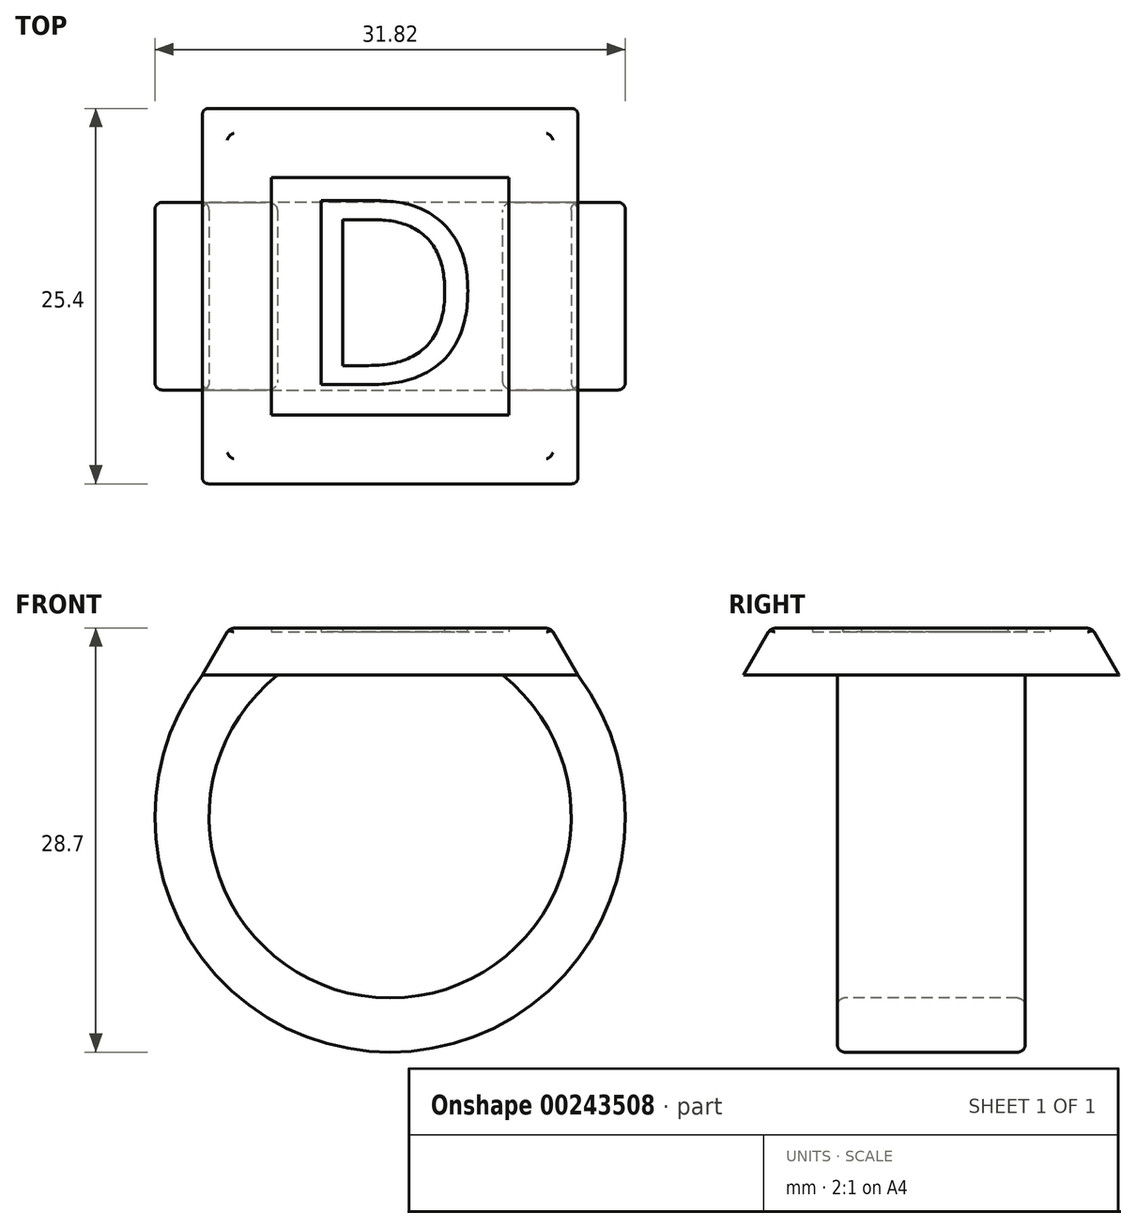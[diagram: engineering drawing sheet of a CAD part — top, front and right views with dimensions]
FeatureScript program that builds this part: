
annotation { "Feature Type Name" : "Feature", "Feature Type Description" : "" }
export const myFeature = defineFeature(function(context is Context, id is Id, definition is map)
    precondition{}
    {
        {
            var Q0;
            Q0=qCreatedBy(makeId("Top.planeOp"),FACE);
            var sketch = newSketch(context, id + "F0", { "sketchPlane" : qUnion([Q0])});
            skLineSegment(sketch, "E0.bottom", {"start": v(-12.7, 12.7) * mm, "end": v(12.7, 12.7) * mm});
            skLineSegment(sketch, "E0.top", {"start": v(-12.7, -12.7) * mm, "end": v(12.7, -12.7) * mm});
            skLineSegment(sketch, "E0.left", {"start": v(-12.7, 12.7) * mm, "end": v(-12.7, -12.7) * mm});
            skLineSegment(sketch, "E0.right", {"start": v(12.7, 12.7) * mm, "end": v(12.7, -12.7) * mm});
            skPoint(sketch, "E0.middle", {"position": v(0, 0) * mm});
            skSolve(sketch);
        }
        {
            var Q0;
            Q0=makeQuery(id+"F0.imprint","IMPRINT",FACE,{"disambiguationData":[TD([[makeQuery(id+"F0.imprint","IMPRINT",EDGE,{"derivedFrom":sQuery(id+"F0.wireOp",EDGE,"E0.bottom")}),-1.0]])]});
            extrude(context, id + "F1", {"entities" : qUnion([Q0]), "depth" : 3.17 * mm, "hasDraft" : true, "draftAngle" : 30 * degree, "draftPullDirection" : true});
        }
        {
            var Q0;
            Q0=qCreatedBy(makeId("Front.planeOp"),FACE);
            var sketch = newSketch(context, id + "F2", { "sketchPlane" : qUnion([Q0])});
            skArc(sketch, "E1", {"start": v(-10.16, 0) * mm, "mid": v(0, -23.56) * mm, "end": v(10.16, 0) * mm});
            skSolve(sketch);
        }
        {
            var Q0;
            Q0=makeQuery(id+"F1.opExtrude","CAP_FACE",FACE,{"disambiguationData":[OSD([sQuery(id+"F0.wireOp",EDGE,"E0.bottom"),sQuery(id+"F0.wireOp",EDGE,"E0.top"),sQuery(id+"F0.wireOp",EDGE,"E0.left"),sQuery(id+"F0.wireOp",EDGE,"E0.right")])],"isStart":true});
            var sketch = newSketch(context, id + "F3", { "sketchPlane" : qUnion([Q0])});
            skLineSegment(sketch, "E2.bottom", {"start": v(-12.7, -6.35) * mm, "end": v(-7.62, -6.35) * mm});
            skLineSegment(sketch, "E2.top", {"start": v(-12.7, 6.35) * mm, "end": v(-7.62, 6.35) * mm});
            skLineSegment(sketch, "E2.left", {"start": v(-12.7, -6.35) * mm, "end": v(-12.7, 6.35) * mm});
            skLineSegment(sketch, "E2.right", {"start": v(-7.62, -6.35) * mm, "end": v(-7.62, 6.35) * mm});
            skPoint(sketch, "E2.middle", {"position": v(-10.16, 0) * mm});
            skSolve(sketch);
        }
        {
            var Q0;
            Q0=makeQuery(id+"F3.imprint","IMPRINT",FACE,{"disambiguationData":[TD([[makeQuery(id+"F3.imprint","IMPRINT",EDGE,{"derivedFrom":sQuery(id+"F3.wireOp",EDGE,"E2.bottom")}),1.0]])]});
            var Q1;
            Q1=sQuery(id+"F2.wireOp",EDGE,"E1");
            sweep(context, id + "F4", {"operationType" : NewBodyOperationType.ADD, "profiles" : qUnion([Q0]), "path" : qUnion([Q1])});
        }
        {
            var Q0;
            Q0=qCreatedBy(makeId("Front.planeOp"),FACE);
            var sketch = newSketch(context, id + "F5", { "sketchPlane" : qUnion([Q0])});
            skLineSegment(sketch, "E3.0", {"start": v(7.62, 0) * mm, "end": v(10.16, 0) * mm});
            skLineSegment(sketch, "E4.0", {"start": v(10.01, -2.54) * mm, "end": v(10.16, 0) * mm});
            skArc(sketch, "E5", {"start": v(10.01, -2.54) * mm, "mid": v(8.9, -1.18) * mm, "end": v(7.62, 0) * mm});
            skSolve(sketch);
        }
        {
            var Q0;
            Q0=makeQuery(id+"F5.imprint","IMPRINT",FACE,{"disambiguationData":[TD([[makeQuery(id+"F5.imprint","IMPRINT",EDGE,{"derivedFrom":sQuery(id+"F5.wireOp",EDGE,"E3.0")}),-1.0]])]});
            extrude(context, id + "F6", {"entities" : qUnion([Q0]), "operationType" : NewBodyOperationType.ADD, "endBound" : BoundingType.SYMMETRIC, "depth" : 12.7 * mm});
        }
        {
            var Q0;
            Q0=makeQuery(id+"F1.opExtrude","CAP_EDGE",EDGE,{"disambiguationData":[OSD([sQuery(id+"F0.wireOp",EDGE,"E0.left")])],"isStart":false});
            var Q1;
            Q1=makeQuery(id+"F1.opExtrude","CAP_EDGE",EDGE,{"disambiguationData":[OSD([sQuery(id+"F0.wireOp",EDGE,"E0.right")])],"isStart":false});
            var Q2;
            Q2=makeQuery(id+"F1.opExtrude","CAP_EDGE",EDGE,{"disambiguationData":[OSD([sQuery(id+"F0.wireOp",EDGE,"E0.top")])],"isStart":false});
            var Q3;
            Q3=makeQuery(id+"F1.opExtrude","CAP_EDGE",EDGE,{"disambiguationData":[OSD([sQuery(id+"F0.wireOp",EDGE,"E0.bottom")])],"isStart":false});
            var Q4;
            Q4=makeQuery(id+"F1.opExtrude","SWEPT_EDGE",EDGE,{"disambiguationData":[OSD([sQuery(id+"F0.wireOp",EDGE,"E0.top"),sQuery(id+"F0.wireOp",EDGE,"E0.right")])]});
            var Q5;
            Q5=makeQuery(id+"F1.opExtrude","SWEPT_EDGE",EDGE,{"disambiguationData":[OSD([sQuery(id+"F0.wireOp",EDGE,"E0.top"),sQuery(id+"F0.wireOp",EDGE,"E0.left")])]});
            var Q6;
            Q6=makeQuery(id+"F1.opExtrude","SWEPT_EDGE",EDGE,{"disambiguationData":[OSD([sQuery(id+"F0.wireOp",EDGE,"E0.bottom"),sQuery(id+"F0.wireOp",EDGE,"E0.left")])]});
            var Q7;
            Q7=makeQuery(id+"F1.opExtrude","SWEPT_EDGE",EDGE,{"disambiguationData":[OSD([sQuery(id+"F0.wireOp",EDGE,"E0.bottom"),sQuery(id+"F0.wireOp",EDGE,"E0.right")])]});
            fillet(context, id + "F7", {"entities" : qUnion([Q0, Q1, Q2, Q3, Q4, Q5, Q6, Q7]), "radius" : 0.5 * mm, "tangentPropagation" : true, "allowEdgeOverflow" : false});
        }
        {
            var Q0;
            Q0=makeQuery(id+"F4.opSweep","SWEPT_EDGE",EDGE,{"disambiguationData":[OSD([sQuery(id+"F2.wireOp",EDGE,"E1"),sQuery(id+"F3.wireOp",EDGE,"E2.bottom"),sQuery(id+"F3.wireOp",EDGE,"E2.right")])]});
            var Q1;
            Q1=makeQuery(id+"F4.opSweep","SWEPT_EDGE",EDGE,{"disambiguationData":[OSD([sQuery(id+"F2.wireOp",EDGE,"E1"),sQuery(id+"F3.wireOp",EDGE,"E2.top"),sQuery(id+"F3.wireOp",EDGE,"E2.right")])]});
            var Q2;
            Q2=makeQuery(id+"F4.opSweep","SWEPT_EDGE",EDGE,{"disambiguationData":[OSD([sQuery(id+"F0.wireOp",EDGE,"E0.left"),sQuery(id+"F2.wireOp",EDGE,"E1"),sQuery(id+"F3.wireOp",EDGE,"E2.top"),sQuery(id+"F3.wireOp",EDGE,"E2.left")])]});
            var Q3;
            Q3=makeQuery(id+"F4.opSweep","SWEPT_EDGE",EDGE,{"disambiguationData":[OSD([sQuery(id+"F0.wireOp",EDGE,"E0.left"),sQuery(id+"F2.wireOp",EDGE,"E1"),sQuery(id+"F3.wireOp",EDGE,"E2.bottom"),sQuery(id+"F3.wireOp",EDGE,"E2.left")])]});
            var Q4;
            Q4=makeQuery(id+"F4.opSweep","CAP_EDGE",EDGE,{"disambiguationData":[OSD([sQuery(id+"F2.wireOp",VERTEX,"E1.end"),sQuery(id+"F3.wireOp",EDGE,"E2.bottom")])],"isStart":false});
            var Q5;
            Q5=makeQuery(id+"F4.opSweep","CAP_EDGE",EDGE,{"disambiguationData":[OSD([sQuery(id+"F2.wireOp",VERTEX,"E1.end"),sQuery(id+"F3.wireOp",EDGE,"E2.top")])],"isStart":false});
            fillet(context, id + "F8", {"entities" : qUnion([Q0, Q1, Q2, Q3, Q4, Q5]), "radius" : 0.5 * mm, "tangentPropagation" : true, "allowEdgeOverflow" : false});
        }
        {
            var Q0;
            Q0=makeQuery(id+"F1.opExtrude","CAP_FACE",FACE,{"disambiguationData":[OSD([sQuery(id+"F0.wireOp",EDGE,"E0.bottom"),sQuery(id+"F0.wireOp",EDGE,"E0.top"),sQuery(id+"F0.wireOp",EDGE,"E0.left"),sQuery(id+"F0.wireOp",EDGE,"E0.right")])],"isStart":false});
            var sketch = newSketch(context, id + "F9", { "sketchPlane" : qUnion([Q0])});
            skLineSegment(sketch, "E6.0", {"start": v(-8.03, 8.03) * mm, "end": v(-8.03, -8.03) * mm});
            skLineSegment(sketch, "E6.1", {"start": v(8.03, 8.03) * mm, "end": v(-8.03, 8.03) * mm});
            skLineSegment(sketch, "E6.2", {"start": v(8.03, -8.03) * mm, "end": v(8.03, 8.03) * mm});
            skLineSegment(sketch, "E6.3", {"start": v(-8.03, -8.03) * mm, "end": v(8.03, -8.03) * mm});
            skSolve(sketch);
        }
        {
            var Q0;
            Q0=makeQuery(id+"F9.imprint","IMPRINT",FACE,{"disambiguationData":[TD([[makeQuery(id+"F9.imprint","IMPRINT",EDGE,{"derivedFrom":sQuery(id+"F9.wireOp",EDGE,"E6.0")}),1.0]])]});
            extrude(context, id + "F10", {"entities" : qUnion([Q0]), "operationType" : NewBodyOperationType.REMOVE, "endBound" : BoundingType.SYMMETRIC, "depth" : 0.48 * mm, "hasDraft" : true, "draftAngle" : 1 * degree});
        }
        {
            var Q0;
            Q0=makeQuery(id+"F10.boolean.opBoolean","COPY",FACE,{"derivedFrom":makeQuery(id+"F10.opExtrude","CAP_FACE",FACE,{"disambiguationData":[OSD([sQuery(id+"F9.wireOp",EDGE,"E6.0"),sQuery(id+"F9.wireOp",EDGE,"E6.1"),sQuery(id+"F9.wireOp",EDGE,"E6.2"),sQuery(id+"F9.wireOp",EDGE,"E6.3")])],"isStart":true})});
            var sketch = newSketch(context, id + "F11", { "sketchPlane" : qUnion([Q0])});
            skText(sketch, "E7", { "text": "D", "fontName": "OpenSans-Regular.ttf"});
            const initialGuessF11  = {"E7": [-0.00636, -0.00596, 1, 0, 0.0125]};
            skSetInitialGuess(sketch, initialGuessF11);
            skSolve(sketch);
        }
        {
            var Q0;
            Q0 = qSketchRegion(id + "F11", true);
            extrude(context, id + "F12", {"entities" : qUnion([Q0]), "operationType" : NewBodyOperationType.ADD, "endBound" : BoundingType.SYMMETRIC, "depth" : 0.53 * mm, "hasDraft" : true, "draftAngle" : 4 * degree});
        }
    });
